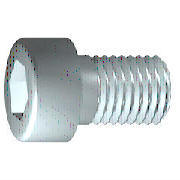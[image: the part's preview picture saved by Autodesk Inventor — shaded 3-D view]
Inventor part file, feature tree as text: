
AUTODESK INVENTOR PART (.ipt)
format: ipt  version: 2023.3 (Build 273359000, 359)  size: 192,512 bytes
history: native  units: mm (DEFAULTED — no unit token found)
features: sketch x2, other x1, extrude x1, plane x1, fillet x1
ambient origin geometry x7: Origin, YZ Plane, XY Plane, X Axis, Y Axis, Z Axis, Center Point
bodies: Solid1 (feature_tree)
feature tree (6):
  other  "Körper"
  extrude  "Loch"  Depth=3.0mm
  plane  "Work Plane1"
  fillet  "Fillet2"  Radius=3.0mm
  sketch  "Skizze1"  dims[d1=8.75mm d2=0.306825mm d3=3.0mm]
  sketch  "Skizze2"  dims[d4=1.3mm d5=60.0deg d6=3.0mm d7=3.0mm d8=2.886751mm d9=5.5mm d10=90.0deg d11=10.0mm d12=0.0mm d13=8.75mm d14=0.0mm d15=0.306725mm d16=0.306725mm d17=0.3mm d19=0.0mm d26=10.0mm d27=45.0deg d28=0.0mm d29=0.0mm d30=0.1mm]
